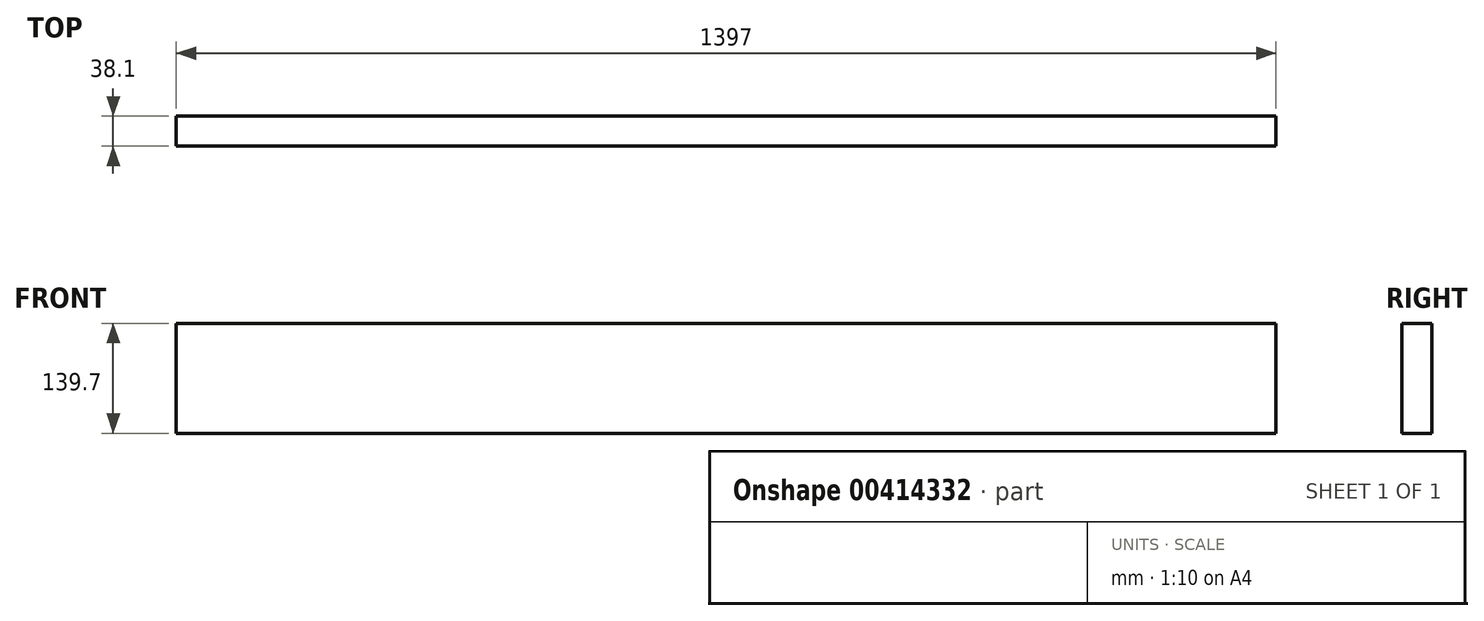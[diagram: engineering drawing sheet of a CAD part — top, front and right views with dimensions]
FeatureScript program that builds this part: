
annotation { "Feature Type Name" : "Feature", "Feature Type Description" : "" }
export const myFeature = defineFeature(function(context is Context, id is Id, definition is map)
    precondition{}
    {
        {
            var Q0;
            Q0=qCreatedBy(makeId("Top.planeOp"),FACE);
            var sketch = newSketch(context, id + "F0", { "sketchPlane" : qUnion([Q0])});
            skLineSegment(sketch, "E0.bottom", {"start": v(698.5, 19.05) * mm, "end": v(-698.5, 19.05) * mm});
            skLineSegment(sketch, "E0.top", {"start": v(698.5, -19.05) * mm, "end": v(-698.5, -19.05) * mm});
            skLineSegment(sketch, "E0.left", {"start": v(698.5, 19.05) * mm, "end": v(698.5, -19.05) * mm});
            skLineSegment(sketch, "E0.right", {"start": v(-698.5, 19.05) * mm, "end": v(-698.5, -19.05) * mm});
            skPoint(sketch, "E0.middle", {"position": v(0, 0) * mm});
            skSolve(sketch);
        }
        {
            var Q0;
            Q0 = qSketchRegion(id + "F0", true);
            extrude(context, id + "F1", {"entities" : qUnion([Q0]), "depth" : 139.7 * mm});
        }
    });
